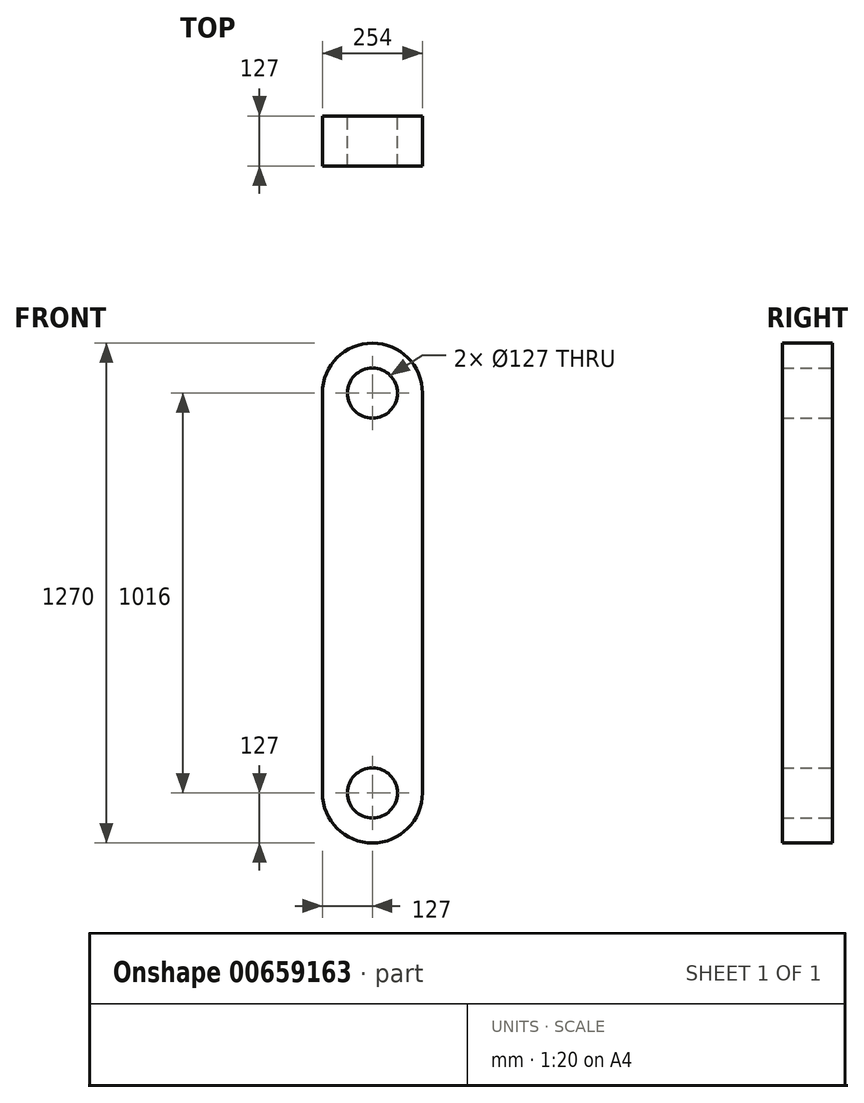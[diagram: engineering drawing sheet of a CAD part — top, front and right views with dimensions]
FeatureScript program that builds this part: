
annotation { "Feature Type Name" : "Feature", "Feature Type Description" : "" }
export const myFeature = defineFeature(function(context is Context, id is Id, definition is map)
    precondition{}
    {
        {
            var Q0;
            Q0=qCreatedBy(makeId("Front.planeOp"),FACE);
            var sketch = newSketch(context, id + "F0", { "sketchPlane" : qUnion([Q0])});
            skLineSegment(sketch, "E0.left", {"start": v(-127, 508) * mm, "end": v(-127, -508) * mm});
            skLineSegment(sketch, "E0.right", {"start": v(127, 508) * mm, "end": v(127, -508) * mm});
            skPoint(sketch, "E0.middle", {"position": v(0, 0) * mm});
            skArc(sketch, "E1", {"start": v(127, 508) * mm, "mid": v(0, 635) * mm, "end": v(-127, 508) * mm});
            skCircle(sketch, "E2", {"center": v(0, 508) * mm, "radius": 63.5 * mm});
            skArc(sketch, "E3", {"start": v(-127, -508) * mm, "mid": v(0, -635) * mm, "end": v(127, -508) * mm});
            skCircle(sketch, "E4", {"center": v(0, -508) * mm, "radius": 63.5 * mm});
            skSolve(sketch);
        }
        {
            var Q0;
            Q0=makeQuery(id+"F0.imprint","IMPRINT",FACE,{"disambiguationData":[TD([[makeQuery(id+"F0.imprint","IMPRINT",EDGE,{"derivedFrom":sQuery(id+"F0.wireOp",EDGE,"E0.left")}),1.0]])]});
            extrude(context, id + "F1", {"entities" : qUnion([Q0]), "depth" : 127 * mm, "offsetDistance" : 25.4 * mm});
        }
    });
